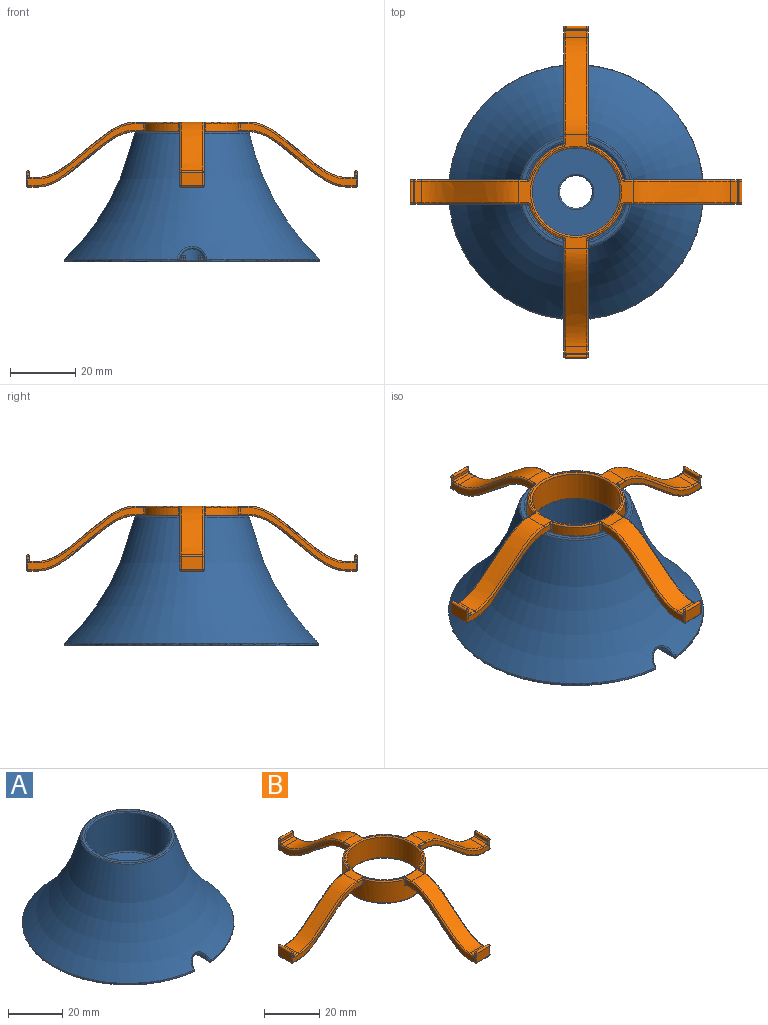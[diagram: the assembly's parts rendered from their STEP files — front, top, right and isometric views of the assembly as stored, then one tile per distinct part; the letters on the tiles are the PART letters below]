
ASSEMBLY  parts=2 mates=1
PART A: 139 faces, bbox 199.6x199.6x76.4 mm
  f0: plane 77.5x77.24mm, normal (0,0,-1), area 4351.1mm2, adj f29,f30,f34,f39,f40,f44,f49,f53
  f1: plane 67.91x67.64mm, normal (0,0,1), area 3205.5mm2, adj f17,f31,f32,f36,f37,f41,f47,f51
  f2: plane 1x0.96mm, normal (0,1,0), area 0.8mm2, adj f28,f29,f37,f38
  f3: plane 1x0.96mm, normal (0,-1,0), area 0.8mm2, adj f48,f49,f56,f57
  f4: plane 1x0.96mm, normal (0,1,0), area 0.8mm2, adj f55,f62,f133,f134
  f5: plane 1x0.96mm, normal (0,-1,0), area 0.8mm2, adj f35,f41,f44,f45
  f6: cylinder r=4mm len=3.84mm, axis (0,1,0), area 2.9mm2, adj f90,f97,f124,f126,f128
  f7: cylinder r=4mm len=3.84mm, axis (0,1,0), area 2.9mm2, adj f66,f67,f132,f133,f136
  f8: cylinder r=4mm len=9mm, axis (0,1,0), area 8.2mm2, adj f102,f103,f111,f112
  f9: cylinder r=4mm len=9mm, axis (0,1,0), area 8.2mm2, adj f28,f31,f34,f35
  f10: cylinder r=5mm len=21mm, axis (0,0,-1), area 550mm2, adj f81,f82,f122
  f11: torus R=92.22mm, axis (0,0,1), area 7428.4mm2, adj f64,f65,f119
  f12: plane 30x30mm, normal (0,0,1), area 611.8mm2, adj f120,f122
  f13: cylinder r=15.5mm len=31mm, axis (0,0,-1), area 1655.6mm2, adj f120,f121
  f14: plane 34.19x34.19mm, normal (0,0,1), area 113.9mm2, adj f119,f121
  f15: cylinder r=4mm len=8.19mm, axis (0,1,0), area 30.4mm2, adj f57,f58,f63,f64,f68,f72,f73,f75
  f16: torus R=92.29mm, axis (0,0,1), area 5316.4mm2, adj f18,f71,f72
  f17: cone r=17.5mm half-angle=45deg, axis (0,0,1), area 1002.6mm2, adj f1,f18,f118
  f18: cylinder r=17.5mm len=35mm, axis (0,0,-1), area 2331.4mm2, adj f16,f17
  f19: bspline ~15.21x12.18mm, area 156.1mm2, adj f67,f74,f82,f89,f90,f118,f130,f138
  f20: plane 1x0.96mm, normal (0,1,0), area 0.8mm2, adj f95,f96,f101,f102
  f21: plane 1x0.96mm, normal (0,-1,0), area 0.8mm2, adj f79,f80,f86,f87
  f22: plane 1x0.96mm, normal (0,1,0), area 0.8mm2, adj f100,f110,f125,f126
  f23: plane 1x0.96mm, normal (0,-1,0), area 0.8mm2, adj f104,f112,f113,f117
  f24: plane 4x1mm, normal (1,0,0), area 4mm2, adj f45,f51,f54,f55
  f25: plane 4x1mm, normal (-1,0,0), area 4mm2, adj f105,f110,f113,f114
  f26: plane 4x1mm, normal (1,0,0), area 4mm2, adj f38,f39,f47,f48
  f27: plane 4x1mm, normal (-1,0,0), area 4mm2, adj f87,f88,f94,f95
  f28: torus R=3.5mm, axis (0,-1,0), area 0.8mm2, adj f2,f9,f30,f32
  f29: cylinder r=0.5mm len=0.96mm, axis (-1,0,0), area 0.8mm2, adj f0,f2,f30,f33
  f30: bspline ~1.22x1.18mm, area 0.8mm2, adj f0,f28,f29,f34
  f31: cylinder r=0.5mm len=9mm, axis (0,1,0), area 8.6mm2, adj f1,f9,f32,f36
  f32: bspline ~1.36x1.07mm, area 1mm2, adj f1,f28,f31,f37
  f33: sphere r=0.5mm, area 0.2mm2, adj f29,f38,f39
  f34: cylinder r=0.5mm len=9mm, axis (0,1,0), area 6.6mm2, adj f0,f9,f30,f40
  f35: torus R=3.5mm, axis (0,-1,0), area 0.8mm2, adj f5,f9,f36,f40
  f36: bspline ~1.21x1.2mm, area 1mm2, adj f1,f31,f35,f41
  f37: cylinder r=0.5mm len=0.66mm, axis (1,0,0), area 0.5mm2, adj f1,f2,f32,f42
  f38: cylinder r=0.5mm len=1mm, axis (0,0,-1), area 0.8mm2, adj f2,f26,f33,f42
  f39: cylinder r=0.5mm len=4mm, axis (0,1,0), area 3.1mm2, adj f0,f26,f33,f43
  f40: bspline ~1.24x1.18mm, area 0.8mm2, adj f0,f34,f35,f44
  f41: cylinder r=0.5mm len=0.66mm, axis (-1,0,0), area 0.5mm2, adj f1,f5,f36,f46
  f42: sphere r=0.5mm, area 0.2mm2, adj f37,f38,f47
  f43: sphere r=0.5mm, area 0.4mm2, adj f39,f48,f49
  f44: cylinder r=0.5mm len=0.96mm, axis (1,0,0), area 0.8mm2, adj f0,f5,f40,f50
  f45: cylinder r=0.5mm len=1mm, axis (0,0,1), area 0.8mm2, adj f5,f24,f46,f50
  f46: sphere r=0.5mm, area 0.4mm2, adj f41,f45,f51
  f47: cylinder r=0.5mm len=4mm, axis (0,1,0), area 3.1mm2, adj f1,f26,f42,f52
  f48: cylinder r=0.5mm len=1mm, axis (0,0,1), area 0.8mm2, adj f3,f26,f43,f52
  f49: cylinder r=0.5mm len=0.96mm, axis (1,0,0), area 0.8mm2, adj f0,f3,f43,f53
  f50: sphere r=0.5mm, area 0.4mm2, adj f44,f45,f54
  f51: cylinder r=0.5mm len=4.35mm, axis (0,-1,0), area 3.3mm2, adj f1,f24,f46,f55,f134
  f52: sphere r=0.5mm, area 0.4mm2, adj f47,f48,f56
  f53: bspline ~1.24x1.18mm, area 0.8mm2, adj f0,f49,f57,f58
  f54: cylinder r=0.5mm len=4mm, axis (0,1,0), area 3.1mm2, adj f0,f24,f50,f59
  f55: cylinder r=0.5mm len=1.35mm, axis (0,0,-1), area 0.9mm2, adj f4,f24,f51,f59,f134
  f56: cylinder r=0.5mm len=0.66mm, axis (-1,0,0), area 0.5mm2, adj f1,f3,f52,f60
  f57: torus R=3.5mm, axis (0,-1,0), area 0.8mm2, adj f3,f15,f53,f60
  f58: cylinder r=0.5mm len=8.19mm, axis (0,1,0), area 6mm2, adj f0,f15,f53,f61
  f59: sphere r=0.5mm, area 0.2mm2, adj f54,f55,f62
  f60: bspline ~1.21x1.2mm, area 1mm2, adj f1,f56,f57,f63
  f61: sphere r=0.5mm, area 0.6mm2, adj f58,f64,f65
  f62: cylinder r=0.5mm len=1.97mm, axis (-1,0,0), area 1mm2, adj f0,f4,f59,f131,f132
  f63: cylinder r=0.5mm len=3.38mm, axis (0,1,0), area 3.2mm2, adj f1,f15,f60,f68
  f64: bspline ~9.08x4.89mm, area 14.9mm2, adj f11,f15,f61,f69
  f65: torus R=38.75mm, axis (0,0,-1), area 280.7mm2, adj f0,f11,f61,f69
  f66: cylinder r=0.5mm len=4.83mm, axis (0,1,0), area 3.2mm2, adj f0,f7,f70,f131
  f67: bspline ~2.36x1.46mm, area 0.3mm2, adj f7,f19,f70,f137
  f68: bspline ~1.55x1.48mm, area 1.4mm2, adj f15,f63,f71,f72
  f69: sphere r=0.5mm, area 0.7mm2, adj f64,f65,f73
  f70: sphere r=0.5mm, area 0mm2, adj f66,f67,f74
  f71: torus R=33.95mm, axis (0,0,-1), area 240.3mm2, adj f1,f16,f68,f75
  f72: bspline ~7.35x2.11mm, area 3.2mm2, adj f15,f16,f68,f75
  f73: cylinder r=0.5mm len=8.19mm, axis (0,1,0), area 6mm2, adj f0,f15,f69,f76
  f74: bspline ~4.55x1.35mm, area 2.8mm2, adj f0,f19,f70,f77
  f75: bspline ~1.61x1.54mm, area 1.4mm2, adj f15,f71,f72,f78
  f76: bspline ~1.22x1.18mm, area 0.8mm2, adj f0,f73,f79,f80
  f77: sphere r=0.5mm, area 0mm2, adj f74,f81,f82
  f78: cylinder r=0.5mm len=3.38mm, axis (0,1,0), area 3.2mm2, adj f1,f15,f75,f83
  f79: torus R=3.5mm, axis (0,-1,0), area 0.8mm2, adj f15,f21,f76,f83
  f80: cylinder r=0.5mm len=0.96mm, axis (1,0,0), area 0.8mm2, adj f0,f21,f76,f84
  f81: torus R=5.5mm, axis (0,0,1), area 15.8mm2, adj f0,f10,f77,f85
  f82: bspline ~13.59x9.32mm, area 7.1mm2, adj f10,f19,f77,f85
  f83: bspline ~1.36x1.07mm, area 1mm2, adj f1,f78,f79,f86
  f84: sphere r=0.5mm, area 0.4mm2, adj f80,f87,f88
  f85: sphere r=0.5mm, area 0mm2, adj f81,f82,f89
  f86: cylinder r=0.5mm len=0.66mm, axis (-1,0,0), area 0.5mm2, adj f1,f21,f83,f91
  f87: cylinder r=0.5mm len=1mm, axis (0,0,-1), area 0.8mm2, adj f21,f27,f84,f91
  f88: cylinder r=0.5mm len=4mm, axis (0,-1,0), area 3.1mm2, adj f0,f27,f84,f92
  f89: bspline ~4.55x1.35mm, area 2.8mm2, adj f0,f19,f85,f93
  f90: bspline ~2.33x1.45mm, area 0.3mm2, adj f6,f19,f93,f129
  f91: sphere r=0.5mm, area 0.4mm2, adj f86,f87,f94
  f92: sphere r=0.5mm, area 0.5mm2, adj f88,f95,f96
  f93: sphere r=0.5mm, area 0mm2, adj f89,f90,f97
  f94: cylinder r=0.5mm len=4mm, axis (0,-1,0), area 3.1mm2, adj f1,f27,f91,f98
  f95: cylinder r=0.5mm len=1mm, axis (0,0,1), area 0.8mm2, adj f20,f27,f92,f98
  f96: cylinder r=0.5mm len=0.96mm, axis (-1,0,0), area 0.8mm2, adj f0,f20,f92,f99
  f97: cylinder r=0.5mm len=4.83mm, axis (0,1,0), area 3.2mm2, adj f0,f6,f93,f123
  f98: sphere r=0.5mm, area 0.5mm2, adj f94,f95,f101
  f99: bspline ~1.24x1.18mm, area 0.8mm2, adj f0,f96,f102,f103
  f100: cylinder r=0.5mm len=1.97mm, axis (-1,0,0), area 1mm2, adj f0,f22,f106,f123,f124
  f101: cylinder r=0.5mm len=0.66mm, axis (1,0,0), area 0.5mm2, adj f1,f20,f98,f107
  f102: torus R=3.5mm, axis (0,-1,0), area 0.8mm2, adj f8,f20,f99,f107
  f103: cylinder r=0.5mm len=9mm, axis (0,1,0), area 6.6mm2, adj f0,f8,f99,f108
  f104: cylinder r=0.5mm len=0.96mm, axis (1,0,0), area 0.8mm2, adj f0,f23,f108,f109
  f105: cylinder r=0.5mm len=4mm, axis (0,-1,0), area 3.1mm2, adj f0,f25,f106,f109
  f106: sphere r=0.5mm, area 0.5mm2, adj f100,f105,f110
  f107: bspline ~1.21x1.2mm, area 1mm2, adj f1,f101,f102,f111
  f108: bspline ~1.22x1.18mm, area 0.8mm2, adj f0,f103,f104,f112
  f109: sphere r=0.5mm, area 0.4mm2, adj f104,f105,f113
  f110: cylinder r=0.5mm len=1.35mm, axis (0,0,1), area 0.9mm2, adj f22,f25,f106,f114,f125
  f111: cylinder r=0.5mm len=9mm, axis (0,1,0), area 8.6mm2, adj f1,f8,f107,f115
  f112: torus R=3.5mm, axis (0,-1,0), area 0.8mm2, adj f8,f23,f108,f115
  f113: cylinder r=0.5mm len=1mm, axis (0,0,-1), area 0.8mm2, adj f23,f25,f109,f116
  f114: cylinder r=0.5mm len=4.35mm, axis (0,1,0), area 3.3mm2, adj f1,f25,f110,f116,f125
  f115: bspline ~1.36x1.07mm, area 1mm2, adj f1,f111,f112,f117
  f116: sphere r=0.5mm, area 0.2mm2, adj f113,f114,f117
  f117: cylinder r=0.5mm len=0.66mm, axis (-1,0,0), area 0.5mm2, adj f1,f23,f115,f116
  f118: bspline ~9.47x7.58mm, area 15mm2, adj f1,f17,f19,f128,f129,f130,f136,f137
  f119: torus R=17.1mm, axis (0,0,-1), area 74.2mm2, adj f11,f14
  f120: torus R=15mm, axis (0,0,1), area 75.6mm2, adj f12,f13
  f121: torus R=16mm, axis (0,0,1), area 77.4mm2, adj f13,f14
  f122: torus R=5.5mm, axis (0,0,1), area 25.6mm2, adj f10,f12
  f123: bspline ~1x1mm, area 0.3mm2, adj f97,f100,f124
  f124: bspline ~0.56x0.53mm, area 0.1mm2, adj f6,f100,f123,f126
  f125: cylinder r=0.5mm len=1.02mm, axis (1,0,0), area 0.7mm2, adj f1,f22,f110,f114,f127
  f126: torus R=3.5mm, axis (0,-1,0), area 0.7mm2, adj f6,f22,f124,f127
  f127: bspline ~1.21x1.2mm, area 1mm2, adj f1,f125,f126,f128
  f128: cylinder r=0.5mm len=2.35mm, axis (0,1,0), area 2.2mm2, adj f1,f6,f118,f127,f129
  f129: sphere r=0.5mm, area 0mm2, adj f90,f118,f128,f130
  f130: bspline ~3.3x1.06mm, area 0.2mm2, adj f19,f118,f129
  f131: bspline ~1x1mm, area 0.3mm2, adj f62,f66,f132
  f132: bspline ~0.64x0.57mm, area 0.1mm2, adj f7,f62,f131,f133
  f133: torus R=3.5mm, axis (0,-1,0), area 0.7mm2, adj f4,f7,f132,f135
  f134: cylinder r=0.5mm len=1.02mm, axis (1,0,0), area 0.7mm2, adj f1,f4,f51,f55,f135
  f135: bspline ~1.36x1.07mm, area 1mm2, adj f1,f133,f134,f136
  f136: cylinder r=0.5mm len=2.35mm, axis (0,1,0), area 2.2mm2, adj f1,f7,f118,f135,f137
  f137: sphere r=0.5mm, area 0mm2, adj f67,f118,f136,f138
  f138: bspline ~3.3x1.06mm, area 0.2mm2, adj f19,f118,f137
PART B: 167 faces, bbox 105.6x105.6x20 mm
  f0: cylinder r=15mm len=30mm, axis (0,0,1), area 752.2mm2, adj f63,f64,f72,f80,f81,f86,f87,f91
  f1: cylinder r=13.5mm len=27mm, axis (0,0,1), area 763.4mm2, adj f164,f165
  f2: plane 29x29mm, normal (0,0,-1), area 44.8mm2, adj f165,f166
  f3: plane 35.05x35.05mm, normal (0,0,1), area 127.5mm2, adj f20,f27,f33,f39,f49,f58,f64,f65
  f4: plane 35.59x19mm, normal (-1,0,0), area 66.2mm2, adj f76,f83,f88,f89,f93,f98,f102,f109
  f5: plane 35.59x19mm, normal (1,0,0), area 66.2mm2, adj f57,f59,f65,f66,f69,f74,f77,f81
  f6: plane 6.5x2.37mm, normal (0,0,-1), area 13.9mm2, adj f21,f82,f92,f93
  f7: plane 35.59x19mm, normal (0,1,0), area 66.2mm2, adj f124,f125,f131,f133,f135,f143,f144,f151
  f8: plane 35.59x19mm, normal (0,-1,0), area 66.2mm2, adj f139,f140,f148,f154,f157,f160,f161,f162
  f9: plane 6.5x2.37mm, normal (0,0,-1), area 13.9mm2, adj f38,f133,f147,f148
  f10: plane 35.59x19mm, normal (-1,0,0), area 66.2mm2, adj f112,f118,f122,f123,f128,f129,f136,f145
  f11: plane 35.59x19mm, normal (1,0,0), area 66.2mm2, adj f95,f99,f103,f106,f107,f111,f114,f119
  f12: plane 6.5x2.37mm, normal (0,0,-1), area 13.9mm2, adj f32,f119,f129,f130
  f13: plane 35.59x19mm, normal (0,1,0), area 66.2mm2, adj f41,f44,f45,f48,f49,f50,f53,f62
  f14: plane 35.59x19mm, normal (0,-1,0), area 66.2mm2, adj f51,f61,f70,f71,f78,f79,f85,f90
  f15: plane 6.5x2.37mm, normal (0,0,-1), area 13.9mm2, adj f26,f62,f79,f80
  f16: plane 6.5x2mm, normal (0,0,1), area 13mm2, adj f20,f69,f84,f98
  f17: plane 6.5x4mm, normal (0,1,0), area 26mm2, adj f56,f57,f67,f76
  f18: plane 6.5x3mm, normal (0,0,-1), area 19.5mm2, adj f21,f66,f67,f83
  f19: plane 6.5x1mm, normal (0,-1,0), area 6.5mm2, adj f56,f57,f76,f84
  f20: bspline ~29.98x17mm, area 228.5mm2, adj f3,f16,f59,f102
  f21: bspline ~29.98x17mm, area 228.5mm2, adj f6,f18,f74,f88
  f22: plane 6.5x2mm, normal (0,0,1), area 13mm2, adj f27,f45,f60,f78
  f23: plane 6.5x4mm, normal (1,0,0), area 26mm2, adj f41,f42,f47,f51
  f24: plane 6.5x3mm, normal (0,0,-1), area 19.5mm2, adj f26,f47,f48,f61
  f25: plane 6.5x1mm, normal (-1,0,0), area 6.5mm2, adj f41,f42,f51,f60
  f26: bspline ~29.98x17mm, area 228.5mm2, adj f15,f24,f53,f71
  f27: bspline ~29.98x17mm, area 228.5mm2, adj f3,f22,f44,f85
  f28: plane 6.5x2mm, normal (0,0,1), area 13mm2, adj f33,f103,f117,f128
  f29: plane 6.5x4mm, normal (0,-1,0), area 26mm2, adj f95,f96,f105,f112
  f30: plane 6.5x3mm, normal (0,0,-1), area 19.5mm2, adj f32,f105,f106,f118
  f31: plane 6.5x1mm, normal (0,1,0), area 6.5mm2, adj f95,f96,f112,f117
  f32: bspline ~29.98x17mm, area 228.5mm2, adj f12,f30,f114,f123
  f33: bspline ~29.98x17mm, area 228.5mm2, adj f3,f28,f99,f136
  f34: plane 6.5x2mm, normal (0,0,1), area 13mm2, adj f39,f151,f158,f162
  f35: plane 6.5x4mm, normal (-1,0,0), area 26mm2, adj f141,f142,f143,f154
  f36: plane 6.5x3mm, normal (0,0,-1), area 19.5mm2, adj f38,f125,f140,f141
  f37: plane 6.5x1mm, normal (1,0,0), area 6.5mm2, adj f142,f143,f154,f158
  f38: bspline ~29.98x17mm, area 228.5mm2, adj f9,f36,f124,f139
  f39: bspline ~29.98x17mm, area 228.5mm2, adj f3,f34,f144,f163
  f40: sphere r=0.5mm, area 0.8mm2, adj f41,f42
  f41: cylinder r=0.5mm len=4mm, axis (0,0,1), area 3.9mm2, adj f13,f23,f25,f40,f43,f50
  f42: cylinder r=0.5mm len=6.5mm, axis (0,-1,0), area 10.2mm2, adj f23,f25,f40,f46
  f43: sphere r=0.5mm, area 0.2mm2, adj f41,f47,f48
  f44: bspline ~40.53x17.5mm, area 27.6mm2, adj f13,f27,f45,f49
  f45: cylinder r=0.5mm len=2mm, axis (1,0,0), area 1.6mm2, adj f13,f22,f44,f50
  f46: sphere r=0.5mm, area 0.8mm2, adj f42,f51
  f47: cylinder r=0.5mm len=6.5mm, axis (0,1,0), area 5.1mm2, adj f23,f24,f43,f52
  f48: cylinder r=0.5mm len=3mm, axis (-1,0,0), area 2.4mm2, adj f13,f24,f43,f53
  f49: cylinder r=0.5mm len=2.62mm, axis (-1,0,0), area 2.1mm2, adj f3,f13,f44,f58
  f50: torus R=1mm, axis (0,-1,0), area 0.8mm2, adj f13,f41,f45,f60
  f51: cylinder r=0.5mm len=4mm, axis (0,0,-1), area 3.9mm2, adj f14,f23,f25,f46,f52,f70
  f52: sphere r=0.5mm, area 0.4mm2, adj f47,f51,f61
  f53: bspline ~40.53x17.5mm, area 27.6mm2, adj f13,f26,f48,f62
  f54: sphere r=0.5mm, area 0.6mm2, adj f56,f57
  f55: sphere r=0.5mm, area 0.2mm2, adj f57,f66,f67
  f56: cylinder r=0.5mm len=6.5mm, axis (1,0,0), area 10.2mm2, adj f17,f19,f54,f68
  f57: cylinder r=0.5mm len=4mm, axis (0,0,-1), area 3.9mm2, adj f5,f17,f19,f54,f55,f77
  f58: torus R=1mm, axis (0,0,1), area 0.7mm2, adj f3,f49,f63,f64
  f59: bspline ~40.53x17.5mm, area 27.6mm2, adj f5,f20,f65,f69
  f60: cylinder r=0.5mm len=6.5mm, axis (0,1,0), area 5.1mm2, adj f22,f25,f50,f70
  f61: cylinder r=0.5mm len=3mm, axis (1,0,0), area 2.4mm2, adj f14,f24,f52,f71
  f62: cylinder r=0.5mm len=2.62mm, axis (1,0,0), area 2mm2, adj f13,f15,f53,f72
  f63: cylinder r=0.5mm len=2mm, axis (0,0,1), area 1.3mm2, adj f0,f13,f58,f72
  f64: torus R=14.5mm, axis (0,0,1), area 11.8mm2, adj f0,f3,f58,f73
  f65: cylinder r=0.5mm len=2.62mm, axis (0,1,0), area 2.1mm2, adj f3,f5,f59,f73
  f66: cylinder r=0.5mm len=3mm, axis (0,1,0), area 2.4mm2, adj f5,f18,f55,f74
  f67: cylinder r=0.5mm len=6.5mm, axis (-1,0,0), area 5.1mm2, adj f17,f18,f55,f75
  f68: sphere r=0.5mm, area 0.9mm2, adj f56,f76
  f69: cylinder r=0.5mm len=2mm, axis (0,-1,0), area 1.6mm2, adj f5,f16,f59,f77
  f70: torus R=1mm, axis (0,-1,0), area 0.8mm2, adj f14,f51,f60,f78
  f71: bspline ~36.57x17.5mm, area 27.6mm2, adj f14,f26,f61,f79
  f72: bspline ~1.22x1.11mm, area 0.8mm2, adj f0,f62,f63,f80
  f73: torus R=1mm, axis (0,0,1), area 0.7mm2, adj f3,f64,f65,f81
  f74: bspline ~36.57x17.5mm, area 27.6mm2, adj f5,f21,f66,f82
  f75: sphere r=0.5mm, area 0.5mm2, adj f67,f76,f83
  f76: cylinder r=0.5mm len=4mm, axis (0,0,1), area 3.9mm2, adj f4,f17,f19,f68,f75,f89
  f77: torus R=1mm, axis (1,0,0), area 0.8mm2, adj f5,f57,f69,f84
  f78: cylinder r=0.5mm len=2mm, axis (-1,0,0), area 1.6mm2, adj f14,f22,f70,f85
  f79: cylinder r=0.5mm len=2.62mm, axis (-1,0,0), area 2mm2, adj f14,f15,f71,f86
  f80: torus R=15.5mm, axis (0,0,1), area 5mm2, adj f0,f15,f72,f86
  f81: cylinder r=0.5mm len=2mm, axis (0,0,1), area 1.3mm2, adj f0,f5,f73,f87
  f82: cylinder r=0.5mm len=2.62mm, axis (0,-1,0), area 2mm2, adj f5,f6,f74,f87
  f83: cylinder r=0.5mm len=3mm, axis (0,-1,0), area 2.4mm2, adj f4,f18,f75,f88
  f84: cylinder r=0.5mm len=6.5mm, axis (-1,0,0), area 5.1mm2, adj f16,f19,f77,f89
  f85: bspline ~40.53x17.5mm, area 27.6mm2, adj f14,f27,f78,f90
  f86: bspline ~1.19x1.19mm, area 0.8mm2, adj f0,f79,f80,f91
  f87: bspline ~1.19x1.19mm, area 0.8mm2, adj f0,f81,f82,f92
  f88: bspline ~40.53x17.5mm, area 27.6mm2, adj f4,f21,f83,f93
  f89: torus R=1mm, axis (1,0,0), area 0.8mm2, adj f4,f76,f84,f98
  f90: cylinder r=0.5mm len=2.62mm, axis (1,0,0), area 2.1mm2, adj f3,f14,f85,f100
  f91: cylinder r=0.5mm len=2mm, axis (0,0,1), area 1.3mm2, adj f0,f14,f86,f100
  f92: torus R=15.5mm, axis (0,0,1), area 5mm2, adj f0,f6,f87,f101
  f93: cylinder r=0.5mm len=2.62mm, axis (0,1,0), area 2mm2, adj f4,f6,f88,f101
  f94: sphere r=0.5mm, area 0.6mm2, adj f95,f96
  f95: cylinder r=0.5mm len=4mm, axis (0,0,1), area 3.9mm2, adj f11,f29,f31,f94,f97,f111
  f96: cylinder r=0.5mm len=6.5mm, axis (-1,0,0), area 10.2mm2, adj f29,f31,f94,f104
  f97: sphere r=0.5mm, area 0.4mm2, adj f95,f105,f106
  f98: cylinder r=0.5mm len=2mm, axis (0,1,0), area 1.6mm2, adj f4,f16,f89,f102
  f99: bspline ~40.53x17.5mm, area 27.6mm2, adj f11,f33,f103,f107
  f100: torus R=1mm, axis (0,0,1), area 0.7mm2, adj f3,f90,f91,f108
  f101: bspline ~1.22x1.11mm, area 0.8mm2, adj f0,f92,f93,f109
  f102: bspline ~40.53x17.5mm, area 27.6mm2, adj f4,f20,f98,f110
  f103: cylinder r=0.5mm len=2mm, axis (0,-1,0), area 1.6mm2, adj f11,f28,f99,f111
  f104: sphere r=0.5mm, area 0.9mm2, adj f96,f112
  f105: cylinder r=0.5mm len=6.5mm, axis (1,0,0), area 5.1mm2, adj f29,f30,f97,f113
  f106: cylinder r=0.5mm len=3mm, axis (0,1,0), area 2.4mm2, adj f11,f30,f97,f114
  f107: cylinder r=0.5mm len=2.62mm, axis (0,1,0), area 2.1mm2, adj f3,f11,f99,f115
  f108: torus R=14.5mm, axis (0,0,1), area 11.8mm2, adj f0,f3,f100,f115
  f109: cylinder r=0.5mm len=2mm, axis (0,0,1), area 1.3mm2, adj f0,f4,f101,f116
  f110: cylinder r=0.5mm len=2.62mm, axis (0,-1,0), area 2.1mm2, adj f3,f4,f102,f116
  f111: torus R=1mm, axis (-1,0,0), area 0.8mm2, adj f11,f95,f103,f117
  f112: cylinder r=0.5mm len=4mm, axis (0,0,-1), area 3.9mm2, adj f10,f29,f31,f104,f113,f122
  f113: sphere r=0.5mm, area 0.4mm2, adj f105,f112,f118
  f114: bspline ~40.53x17.5mm, area 27.6mm2, adj f11,f32,f106,f119
  f115: torus R=1mm, axis (0,0,1), area 0.7mm2, adj f3,f107,f108,f120
  f116: torus R=1mm, axis (0,0,1), area 0.7mm2, adj f3,f109,f110,f121
  f117: cylinder r=0.5mm len=6.5mm, axis (1,0,0), area 5.1mm2, adj f28,f31,f111,f122
  f118: cylinder r=0.5mm len=3mm, axis (0,-1,0), area 2.4mm2, adj f10,f30,f113,f123
  f119: cylinder r=0.5mm len=2.62mm, axis (0,-1,0), area 2mm2, adj f11,f12,f114,f126
  f120: cylinder r=0.5mm len=2mm, axis (0,0,1), area 1.3mm2, adj f0,f11,f115,f126
  f121: torus R=14.5mm, axis (0,0,1), area 11.8mm2, adj f0,f3,f116,f127
  f122: torus R=1mm, axis (-1,0,0), area 0.8mm2, adj f10,f112,f117,f128
  f123: bspline ~36.57x17.5mm, area 27.6mm2, adj f10,f32,f118,f129
  f124: bspline ~36.57x17.5mm, area 27.6mm2, adj f7,f38,f125,f133
  f125: cylinder r=0.5mm len=3mm, axis (-1,0,0), area 2.4mm2, adj f7,f36,f124,f134
  f126: bspline ~1.22x1.11mm, area 0.8mm2, adj f0,f119,f120,f130
  f127: torus R=1mm, axis (0,0,1), area 0.7mm2, adj f3,f121,f131,f135
  f128: cylinder r=0.5mm len=2mm, axis (0,1,0), area 1.6mm2, adj f10,f28,f122,f136
  f129: cylinder r=0.5mm len=2.62mm, axis (0,1,0), area 2mm2, adj f10,f12,f123,f137
  f130: torus R=15.5mm, axis (0,0,1), area 5mm2, adj f0,f12,f126,f137
  f131: cylinder r=0.5mm len=2mm, axis (0,0,1), area 1.3mm2, adj f0,f7,f127,f138
  f132: sphere r=0.5mm, area 0.8mm2, adj f142,f143
  f133: cylinder r=0.5mm len=2.62mm, axis (1,0,0), area 2mm2, adj f7,f9,f124,f138
  f134: sphere r=0.5mm, area 0.5mm2, adj f125,f141,f143
  f135: cylinder r=0.5mm len=2.62mm, axis (-1,0,0), area 2.1mm2, adj f3,f7,f127,f144
  f136: bspline ~40.53x17.5mm, area 27.6mm2, adj f10,f33,f128,f145
  f137: bspline ~1.19x1.19mm, area 0.8mm2, adj f0,f129,f130,f146
  f138: bspline ~1.19x1.19mm, area 0.8mm2, adj f0,f131,f133,f147
  f139: bspline ~40.53x17.5mm, area 27.6mm2, adj f8,f38,f140,f148
  f140: cylinder r=0.5mm len=3mm, axis (1,0,0), area 2.4mm2, adj f8,f36,f139,f149
  f141: cylinder r=0.5mm len=6.5mm, axis (0,-1,0), area 5.1mm2, adj f35,f36,f134,f149
  f142: cylinder r=0.5mm len=6.5mm, axis (0,1,0), area 10.2mm2, adj f35,f37,f132,f150
  f143: cylinder r=0.5mm len=4mm, axis (0,0,-1), area 3.9mm2, adj f7,f35,f37,f132,f134,f155
  f144: bspline ~40.53x17.5mm, area 27.6mm2, adj f7,f39,f135,f151
  f145: cylinder r=0.5mm len=2.62mm, axis (0,-1,0), area 2.1mm2, adj f3,f10,f136,f152
  f146: cylinder r=0.5mm len=2mm, axis (0,0,1), area 1.3mm2, adj f0,f10,f137,f152
  f147: torus R=15.5mm, axis (0,0,1), area 5mm2, adj f0,f9,f138,f153
  f148: cylinder r=0.5mm len=2.62mm, axis (-1,0,0), area 2mm2, adj f8,f9,f139,f153
  f149: sphere r=0.5mm, area 0.4mm2, adj f140,f141,f154
  f150: sphere r=0.5mm, area 0.8mm2, adj f142,f154
  f151: cylinder r=0.5mm len=2mm, axis (1,0,0), area 1.6mm2, adj f7,f34,f144,f155
  f152: torus R=1mm, axis (0,0,1), area 0.7mm2, adj f3,f145,f146,f156
  f153: bspline ~1.22x1.11mm, area 0.8mm2, adj f0,f147,f148,f157
  f154: cylinder r=0.5mm len=4mm, axis (0,0,1), area 3.9mm2, adj f8,f35,f37,f149,f150,f160
  f155: torus R=1mm, axis (0,1,0), area 0.8mm2, adj f7,f143,f151,f158
  f156: torus R=14.5mm, axis (0,0,1), area 11.8mm2, adj f0,f3,f152,f159
  f157: cylinder r=0.5mm len=2mm, axis (0,0,1), area 1.3mm2, adj f0,f8,f153,f159
  f158: cylinder r=0.5mm len=6.5mm, axis (0,-1,0), area 5.1mm2, adj f34,f37,f155,f160
  f159: torus R=1mm, axis (0,0,1), area 0.7mm2, adj f3,f156,f157,f161
  f160: torus R=1mm, axis (0,1,0), area 0.8mm2, adj f8,f154,f158,f162
  f161: cylinder r=0.5mm len=2.62mm, axis (1,0,0), area 2.1mm2, adj f3,f8,f159,f163
  f162: cylinder r=0.5mm len=2mm, axis (-1,0,0), area 1.6mm2, adj f8,f34,f160,f163
  f163: bspline ~40.53x17.5mm, area 27.6mm2, adj f8,f39,f161,f162
  f164: torus R=14mm, axis (0,0,1), area 67.5mm2, adj f1,f3
  f165: torus R=14mm, axis (0,0,1), area 67.5mm2, adj f1,f2
  f166: torus R=14.5mm, axis (0,0,1), area 73.1mm2, adj f0,f2
PLACE A at identity
PLACE B t=(0,0,23)mm
MATE fastened B.f0 <-> A.f11  axis (0,0,1) through (0,0,23)mm
